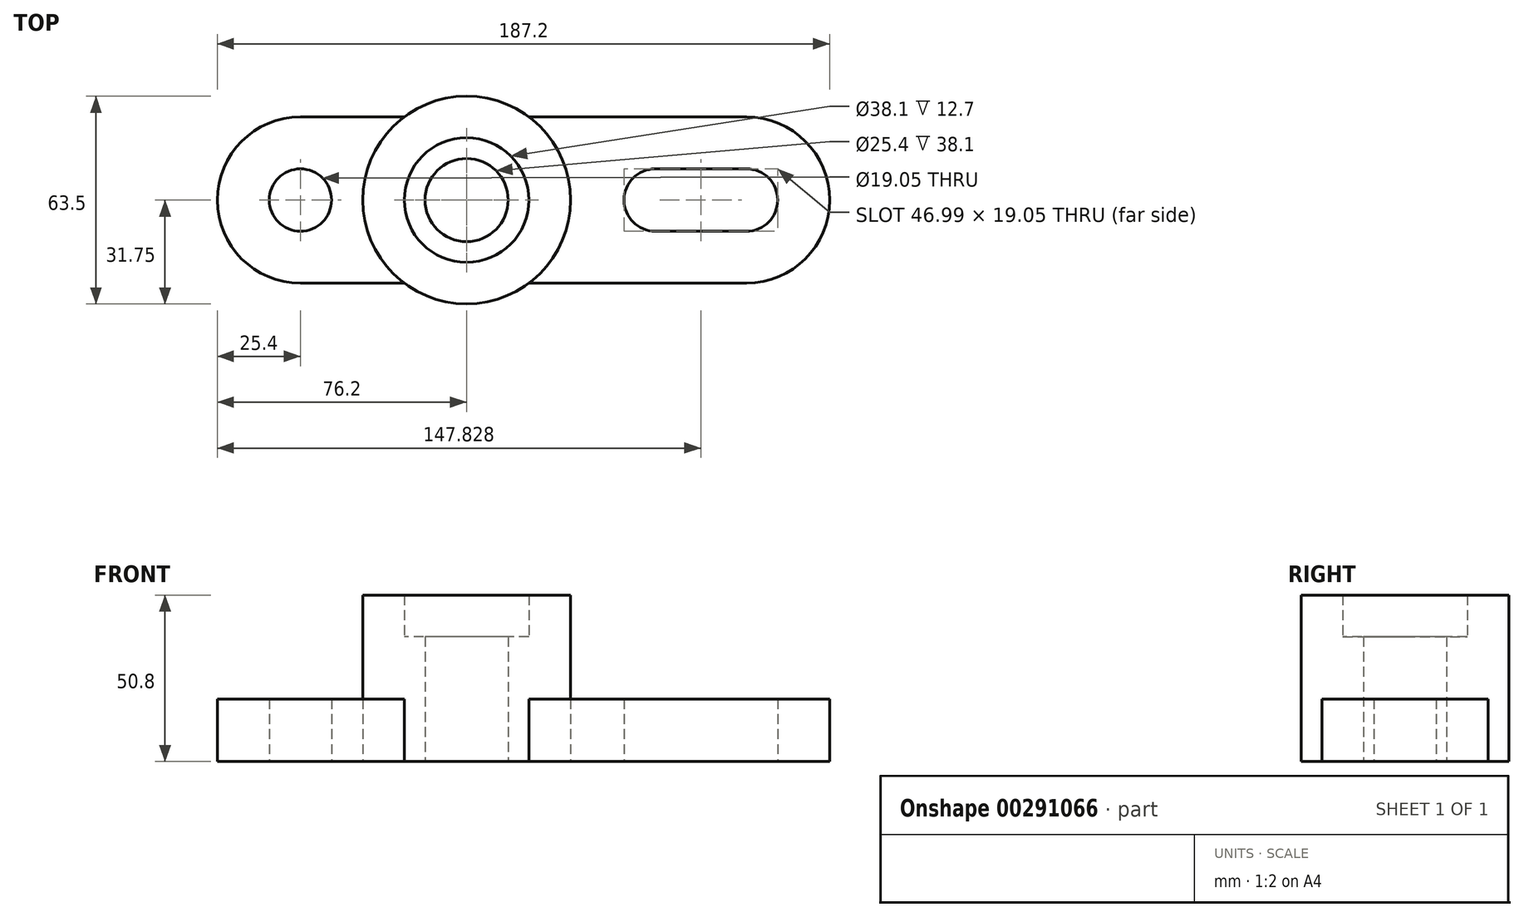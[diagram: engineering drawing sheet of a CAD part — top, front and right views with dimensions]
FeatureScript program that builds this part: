
annotation { "Feature Type Name" : "Feature", "Feature Type Description" : "" }
export const myFeature = defineFeature(function(context is Context, id is Id, definition is map)
    precondition{}
    {
        {
            var Q0;
            Q0=qCreatedBy(makeId("Top.planeOp"),FACE);
            var sketch = newSketch(context, id + "F0", { "sketchPlane" : qUnion([Q0])});
            skCircle(sketch, "E0", {"center": v(0, 0) * mm, "radius": 31.75 * mm});
            skArc(sketch, "E1", {"start": v(-50.8, 25.4) * mm, "mid": v(-76.2, 0) * mm, "end": v(-50.8, -25.4) * mm});
            skArc(sketch, "E2", {"start": v(85.6, -25.4) * mm, "mid": v(111, 0) * mm, "end": v(85.6, 25.4) * mm});
            skLineSegment(sketch, "E3", {"start": v(-50.8, 25.4) * mm, "end": v(-19.05, 25.4) * mm});
            skLineSegment(sketch, "E4", {"start": v(85.6, 25.4) * mm, "end": v(19.05, 25.4) * mm});
            skLineSegment(sketch, "E5", {"start": v(-50.8, -25.4) * mm, "end": v(-19.05, -25.4) * mm});
            skLineSegment(sketch, "E6", {"start": v(85.6, -25.4) * mm, "end": v(19.05, -25.4) * mm});
            skArc(sketch, "E7", {"start": v(85.6, -9.53) * mm, "mid": v(95.12, 0) * mm, "end": v(85.6, 9.52) * mm});
            skArc(sketch, "E8", {"start": v(57.66, 9.52) * mm, "mid": v(48.13, 0) * mm, "end": v(57.66, -9.53) * mm});
            skCircle(sketch, "E9", {"center": v(-50.8, 0) * mm, "radius": 9.53 * mm});
            skLineSegment(sketch, "E10", {"start": v(57.66, 9.53) * mm, "end": v(85.6, 9.52) * mm});
            skLineSegment(sketch, "E11", {"start": v(57.66, -9.53) * mm, "end": v(85.6, -9.53) * mm});
            skCircle(sketch, "E12", {"center": v(0, 0) * mm, "radius": 19.05 * mm});
            skCircle(sketch, "E13", {"center": v(0, 0) * mm, "radius": 12.7 * mm});
            skPoint(sketch, "E14", {"position": v(31.75, 0) * mm});
            skPoint(sketch, "E15", {"position": v(111, 0) * mm});
            skPoint(sketch, "E16", {"position": v(95.12, 0) * mm});
            skSolve(sketch);
        }
        {
            var Q0;
            Q0=makeQuery(id+"F0.imprint","IMPRINT",FACE,{"disambiguationData":[TD([[makeQuery(id+"F0.imprint","IMPRINT",EDGE,{"derivedFrom":sQuery(id+"F0.wireOp",EDGE,"E1")}),1.0]])]});
            var Q1;
            Q1=makeQuery(id+"F0.imprint","IMPRINT",FACE,{"disambiguationData":[TD([[makeQuery(id+"F0.imprint","IMPRINT",EDGE,{"derivedFrom":sQuery(id+"F0.wireOp",EDGE,"E2")}),1.0]])]});
            extrude(context, id + "F1", {"entities" : qUnion([Q0, Q1]), "depth" : 19.05 * mm});
        }
        {
            var Q0;
            Q0=makeQuery(id+"F0.imprint","IMPRINT",FACE,{"disambiguationData":[TD([[makeQuery(id+"F0.imprint","IMPRINT",EDGE,{"derivedFrom":sQuery(id+"F0.wireOp",EDGE,"E12")}),-1.0]])]});
            extrude(context, id + "F2", {"entities" : qUnion([Q0]), "depth" : 50.8 * mm});
        }
        {
            var Q0;
            Q0=makeQuery(id+"F0.imprint","IMPRINT",FACE,{"disambiguationData":[TD([[makeQuery(id+"F0.imprint","IMPRINT",EDGE,{"derivedFrom":sQuery(id+"F0.wireOp",EDGE,"E12")}),1.0]])]});
            extrude(context, id + "F3", {"entities" : qUnion([Q0]), "operationType" : NewBodyOperationType.ADD, "depth" : 38.1 * mm});
        }
    });
